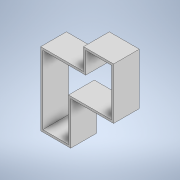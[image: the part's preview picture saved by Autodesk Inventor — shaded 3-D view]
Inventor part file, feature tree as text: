
AUTODESK INVENTOR PART (.ipt)
format: ipt  version: 2022 (Build 260153000, 153)  size: 109,568 bytes
history: native  units: in
note: dims shown in document units (in); Inventor stores cm internally (conversion verified against a paired STEP export)
features: extrude x1, sketch x1
ambient origin geometry x8: Origin, YZ Plane, XZ Plane, XY Plane, X Axis, Y Axis, Z Axis, Center Point
bodies: Solid1 (feature_tree)
feature tree (2):
  extrude  "Extrusion1"  Depth=6.0in TaperAngle=0.0deg
  sketch  "Sketch1"  dims[d6=0.5in d7=6.0in d8=0.0in]
